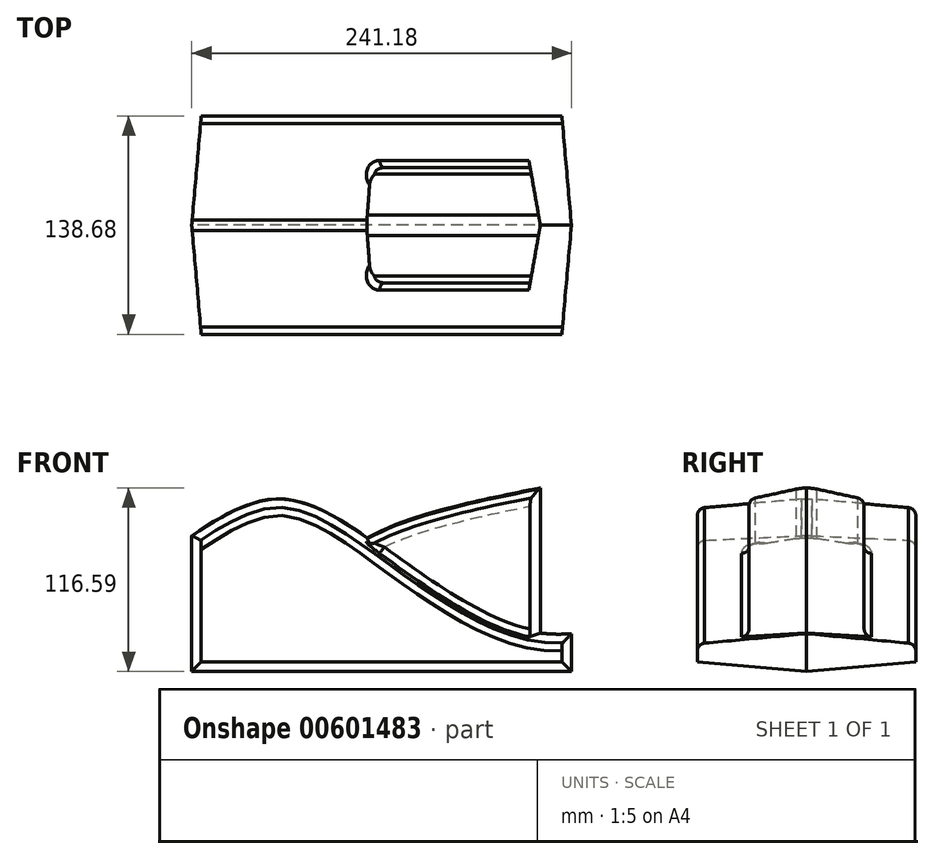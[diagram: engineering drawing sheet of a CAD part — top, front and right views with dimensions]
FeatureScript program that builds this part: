
annotation { "Feature Type Name" : "Feature", "Feature Type Description" : "" }
export const myFeature = defineFeature(function(context is Context, id is Id, definition is map)
    precondition{}
    {
        {
            var Q0;
            Q0=qCreatedBy(makeId("Front.planeOp"),FACE);
            var sketch = newSketch(context, id + "F0", { "sketchPlane" : qUnion([Q0])});
            skFitSpline(sketch, "E0", {"points": [v(-130.14, 24.44) * mm, v(-65.43, 52.81) * mm, v(8.12, 14.18) * mm, v(90.51, -31.03) * mm, v(145.54, -28.83) * mm], "startDerivative": vector(265.05, 180.53) * mm, "endDerivative": vector(247.24, 47.17) * mm});
            skLineSegment(sketch, "E1.top", {"start": v(-122.73, -56.89) * mm, "end": v(118.45, -56.89) * mm});
            skLineSegment(sketch, "E1.left", {"start": v(-122.73, 29.46) * mm, "end": v(-122.73, -56.89) * mm});
            skLineSegment(sketch, "E1.right", {"start": v(118.45, -32.92) * mm, "end": v(118.45, -56.89) * mm});
            skSolve(sketch);
        }
        {
            var Q0;
            Q0=makeQuery(id+"F0.imprint","IMPRINT",FACE,{"disambiguationData":[TD([[makeQuery(id+"F0.imprint","IMPRINT",EDGE,{"derivedFrom":sQuery(id+"F0.wireOp",EDGE,"E0")}),-1.0]])]});
            extrude(context, id + "F1", {"entities" : qUnion([Q0]), "depth" : 138.68 * mm, "offsetDistance" : 25.4 * mm, "hasDraft" : true, "draftAngle" : 5 * degree, "draftPullDirection" : true, "symmetric" : true});
        }
        {
            var Q0;
            Q0=qCreatedBy(makeId("Front.planeOp"),FACE);
            var sketch = newSketch(context, id + "F2", { "sketchPlane" : qUnion([Q0])});
            skFitSpline(sketch, "E2", {"points": [v(-48.74, 5.06) * mm, v(9.28, 37.92) * mm, v(132.93, 67.15) * mm], "startDerivative": vector(117.06, 77.27) * mm, "endDerivative": vector(171.12, 36.82) * mm});
            skLineSegment(sketch, "E3.top", {"start": v(-44.6, -49.66) * mm, "end": v(98.7, -49.66) * mm});
            skLineSegment(sketch, "E3.left", {"start": v(-44.6, 7.83) * mm, "end": v(-44.6, -49.66) * mm});
            skLineSegment(sketch, "E3.right", {"start": v(98.7, 60.3) * mm, "end": v(98.7, -49.66) * mm});
            skSolve(sketch);
        }
        {
            var Q0;
            Q0=makeQuery(id+"F2.imprint","IMPRINT",FACE,{"disambiguationData":[TD([[makeQuery(id+"F2.imprint","IMPRINT",EDGE,{"derivedFrom":sQuery(id+"F2.wireOp",EDGE,"E2")}),-1.0]])]});
            extrude(context, id + "F3", {"entities" : qUnion([Q0]), "operationType" : NewBodyOperationType.ADD, "depth" : 73.15 * mm, "offsetDistance" : 25.4 * mm, "hasDraft" : true, "draftAngle" : 10 * degree, "draftPullDirection" : true, "symmetric" : true});
        }
        {
            var Q0;
            Q0=makeQuery(id+"F3.opExtrude","CAP_EDGE",EDGE,{"disambiguationData":[OSD([sQuery(id+"F2.wireOp",EDGE,"E2")])],"isStart":false});
            var Q1;
            Q1=makeQuery(id+"F3.boolean.opBoolean","INTERSECT",EDGE,{"derivedFrom":[makeQuery(id+"F1.*.split.splitOp","SPLIT",FACE,{"derivedFrom":makeQuery(id+"F1.opExtrude","SWEPT_FACE",FACE,{"disambiguationData":[OSD([sQuery(id+"F0.wireOp",EDGE,"E0")])]})}),makeQuery(id+"F3.opExtrude","CAP_FACE",FACE,{"disambiguationData":[OSD([sQuery(id+"F2.wireOp",EDGE,"E2"),sQuery(id+"F2.wireOp",EDGE,"E3.top"),sQuery(id+"F2.wireOp",EDGE,"E3.left"),sQuery(id+"F2.wireOp",EDGE,"E3.right")])],"isStart":false})]});
            var Q2;
            Q2=makeQuery(id+"F3.opExtrude","CAP_EDGE",EDGE,{"disambiguationData":[OSD([sQuery(id+"F2.wireOp",EDGE,"E2")])],"isStart":true});
            var Q3;
            Q3=makeQuery(id+"F3.boolean.opBoolean","INTERSECT",EDGE,{"derivedFrom":[makeQuery(id+"F1.*.split.splitOp","SPLIT",FACE,{"derivedFrom":makeQuery(id+"F1.opExtrude","SWEPT_FACE",FACE,{"disambiguationData":[OSD([sQuery(id+"F0.wireOp",EDGE,"E0")])]}),"isFromBackBody":true}),makeQuery(id+"F3.opExtrude","CAP_FACE",FACE,{"disambiguationData":[OSD([sQuery(id+"F2.wireOp",EDGE,"E2"),sQuery(id+"F2.wireOp",EDGE,"E3.top"),sQuery(id+"F2.wireOp",EDGE,"E3.left"),sQuery(id+"F2.wireOp",EDGE,"E3.right")])],"isStart":true})]});
            var Q4;
            Q4=makeQuery(id+"F1.opExtrude","CAP_EDGE",EDGE,{"disambiguationData":[OSD([sQuery(id+"F0.wireOp",EDGE,"E0")])],"isStart":false});
            var Q5;
            Q5=makeQuery(id+"F1.opExtrude","CAP_EDGE",EDGE,{"disambiguationData":[OSD([sQuery(id+"F0.wireOp",EDGE,"E0")])],"isStart":true});
            fillet(context, id + "F4", {"entities" : qUnion([Q0, Q1, Q2, Q3, Q4, Q5]), "radius" : 5.08 * mm, "tangentPropagation" : true, "allowEdgeOverflow" : false});
        }
        {
            var Q0;
            {var subQ0=makeQuery(id+"F1.opExtrude","SWEPT_FACE",FACE,{"disambiguationData":[OSD([sQuery(id+"F0.wireOp",EDGE,"E0")])]});Q0=makeQuery(id+"F3.boolean.opBoolean","SPLIT",EDGE,{"disambiguationData":[TD([makeQuery(id+"F1.opExtrude","SWEPT_FACE",FACE,{"disambiguationData":[OSD([sQuery(id+"F0.wireOp",EDGE,"E1.left")])]})])],"derivedFrom":makeQuery(id+"F1.*.booleanUnion.opBoolean","MERGE",EDGE,{"derivedFrom":[makeQuery(id+"F1.*.split.splitOp","SPLIT_SURFACE_INTERSECT",EDGE,{"derivedFrom":[subQ0]}),makeQuery(id+"F1.*.split.splitOp","SPLIT_SURFACE_INTERSECT",EDGE,{"derivedFrom":[subQ0],"isFromBackBody":true})]})});}
            var Q1;
            {var subQ0=makeQuery(id+"F3.opExtrude","SWEPT_FACE",FACE,{"disambiguationData":[OSD([sQuery(id+"F2.wireOp",EDGE,"E2")])]});var subQ1=makeQuery(id+"F1.opExtrude","SWEPT_FACE",FACE,{"disambiguationData":[OSD([sQuery(id+"F0.wireOp",EDGE,"E0")])]});Q1=makeQuery(id+"F4.opFillet","BLEND_EDGE",EDGE,{"blendedFrom":[makeQuery(id+"F3.boolean.opBoolean","INTERSECT",EDGE,{"derivedFrom":[makeQuery(id+"F1.*.split.splitOp","SPLIT",FACE,{"derivedFrom":subQ1}),makeQuery(id+"F3.*.split.splitOp","SPLIT",FACE,{"derivedFrom":subQ0})]}),makeQuery(id+"F3.boolean.opBoolean","INTERSECT",EDGE,{"derivedFrom":[makeQuery(id+"F1.*.split.splitOp","SPLIT",FACE,{"derivedFrom":subQ1,"isFromBackBody":true}),makeQuery(id+"F3.*.split.splitOp","SPLIT",FACE,{"derivedFrom":subQ0,"isFromBackBody":true})]})],"blendedInto":[]});}
            var Q2;
            {var subQ0=makeQuery(id+"F3.opExtrude","SWEPT_FACE",FACE,{"disambiguationData":[OSD([sQuery(id+"F2.wireOp",EDGE,"E2")])]});Q2=makeQuery(id+"F3.*.booleanUnion.opBoolean","MERGE",EDGE,{"derivedFrom":[makeQuery(id+"F3.*.split.splitOp","SPLIT_SURFACE_INTERSECT",EDGE,{"derivedFrom":[subQ0]}),makeQuery(id+"F3.*.split.splitOp","SPLIT_SURFACE_INTERSECT",EDGE,{"derivedFrom":[subQ0],"isFromBackBody":true})]});}
            fillet(context, id + "F5", {"entities" : qUnion([Q0, Q1, Q2]), "radius" : 38.1 * mm, "tangentPropagation" : true, "allowEdgeOverflow" : false});
        }
    });
